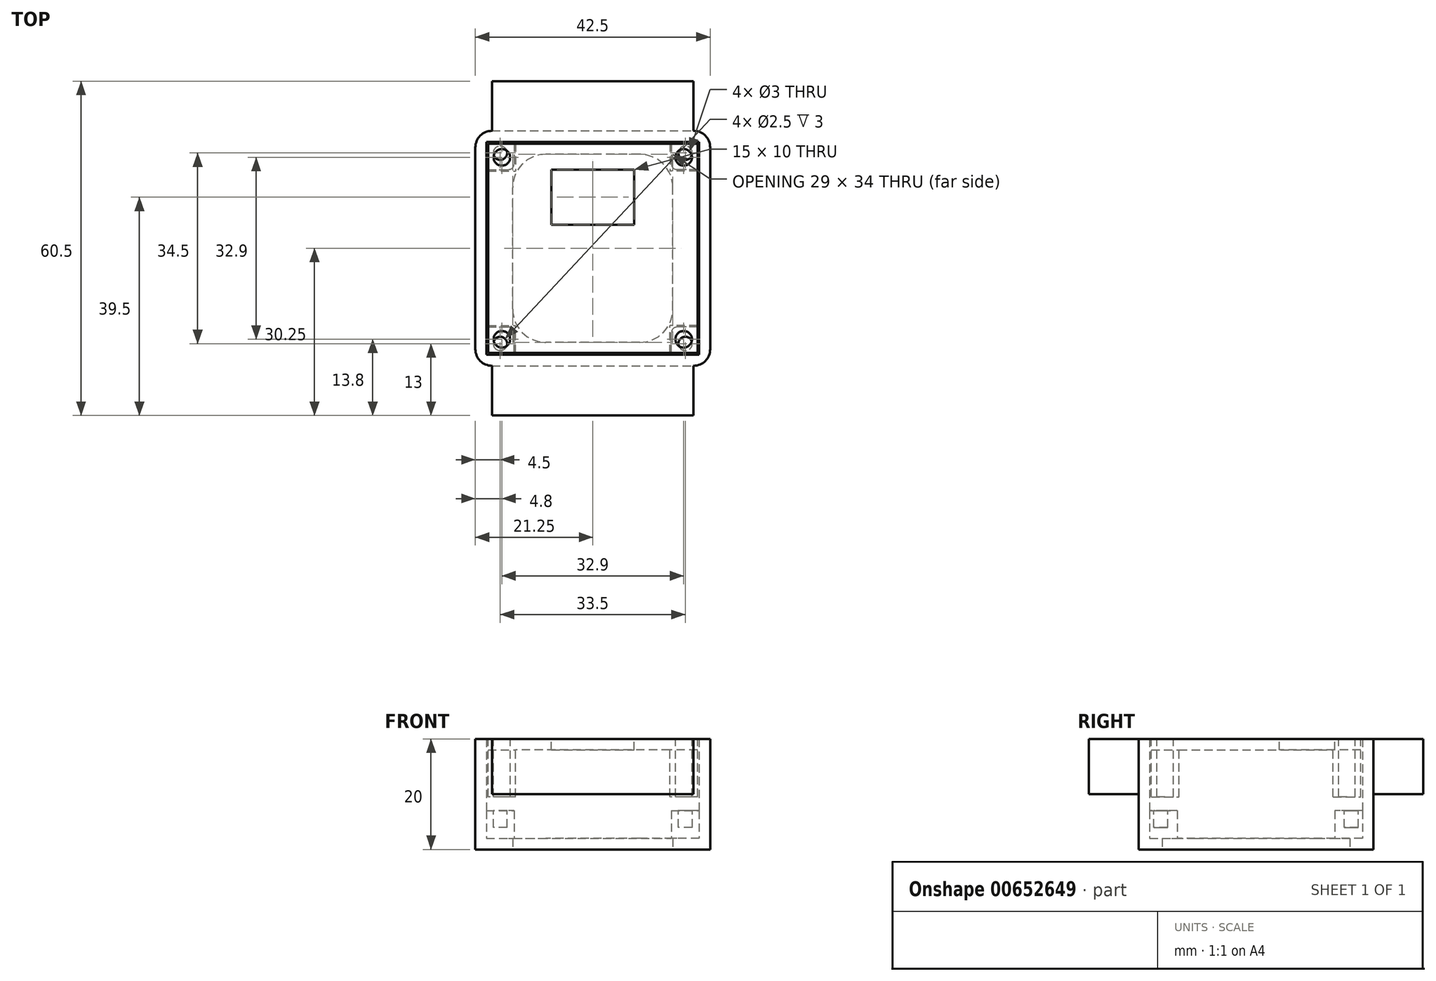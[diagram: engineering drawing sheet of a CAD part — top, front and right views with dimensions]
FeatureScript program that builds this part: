
annotation { "Feature Type Name" : "Feature", "Feature Type Description" : "" }
export const myFeature = defineFeature(function(context is Context, id is Id, definition is map)
    precondition{}
    {
        {
            var Q0;
            Q0=qCreatedBy(makeId("Top.planeOp"),FACE);
            var sketch = newSketch(context, id + "F0", { "sketchPlane" : qUnion([Q0])});
            skLineSegment(sketch, "E0.bottom", {"start": v(19.25, -19.25) * mm, "end": v(-19.25, -19.25) * mm});
            skLineSegment(sketch, "E0.top", {"start": v(19.25, 19.25) * mm, "end": v(-19.25, 19.25) * mm});
            skLineSegment(sketch, "E0.left", {"start": v(19.25, -19.25) * mm, "end": v(19.25, 19.25) * mm});
            skLineSegment(sketch, "E0.right", {"start": v(-19.25, -19.25) * mm, "end": v(-19.25, 19.25) * mm});
            skPoint(sketch, "E0.middle", {"position": v(0, 0) * mm});
            skLineSegment(sketch, "E1.bottom", {"start": v(8.5, -17) * mm, "end": v(-8.5, -17) * mm});
            skLineSegment(sketch, "E1.top", {"start": v(8.5, 17) * mm, "end": v(-8.5, 17) * mm});
            skLineSegment(sketch, "E1.left", {"start": v(14.5, -11) * mm, "end": v(14.5, 11) * mm});
            skLineSegment(sketch, "E1.right", {"start": v(-14.5, -11) * mm, "end": v(-14.5, 11) * mm});
            skLineSegment(sketch, "E2.0", {"start": v(-21.25, -21.25) * mm, "end": v(-21.25, 21.25) * mm});
            skLineSegment(sketch, "E2.1", {"start": v(21.25, -21.25) * mm, "end": v(-21.25, -21.25) * mm});
            skLineSegment(sketch, "E2.2", {"start": v(21.25, -21.25) * mm, "end": v(21.25, 21.25) * mm});
            skLineSegment(sketch, "E2.3", {"start": v(21.25, 21.25) * mm, "end": v(-21.25, 21.25) * mm});
            skPoint(sketch, "E3.visualSharp", {"position": v(-14.5, 17) * mm});
            skArc(sketch, "E3.filletArc", {"start": v(-8.5, 17) * mm, "mid": v(-12.74, 15.24) * mm, "end": v(-14.5, 11) * mm});
            skPoint(sketch, "E4.visualSharp", {"position": v(14.5, 17) * mm});
            skArc(sketch, "E4.filletArc", {"start": v(14.5, 11) * mm, "mid": v(12.74, 15.24) * mm, "end": v(8.5, 17) * mm});
            skPoint(sketch, "E5.visualSharp", {"position": v(14.5, -17) * mm});
            skArc(sketch, "E5.filletArc", {"start": v(8.5, -17) * mm, "mid": v(12.74, -15.24) * mm, "end": v(14.5, -11) * mm});
            skPoint(sketch, "E6.visualSharp", {"position": v(-14.5, -17) * mm});
            skArc(sketch, "E6.filletArc", {"start": v(-14.5, -11) * mm, "mid": v(-12.74, -15.24) * mm, "end": v(-8.5, -17) * mm});
            skSolve(sketch);
        }
        {
            var Q0;
            Q0 = qSketchRegion(id + "F0", true);
            var Q1;
            Q1=makeQuery(id+"F0.imprint","IMPRINT",FACE,{"disambiguationData":[TD([[makeQuery(id+"F0.imprint","IMPRINT",EDGE,{"derivedFrom":sQuery(id+"F0.wireOp",EDGE,"E0.bottom")}),-1.0]])]});
            extrude(context, id + "F1", {"entities" : qUnion([Q0, Q1]), "depth" : 2 * mm, "offsetDistance" : 25 * mm});
        }
        {
            var Q0;
            Q0=makeQuery(id+"F0.imprint","IMPRINT",FACE,{"disambiguationData":[TD([[makeQuery(id+"F0.imprint","IMPRINT",EDGE,{"derivedFrom":sQuery(id+"F0.wireOp",EDGE,"E0.bottom")}),1.0]])]});
            extrude(context, id + "F2", {"entities" : qUnion([Q0]), "operationType" : NewBodyOperationType.ADD, "depth" : 15 * mm, "offsetDistance" : 25 * mm});
        }
        {
            var Q0;
            Q0=makeQuery(id+"F1.opExtrude","CAP_FACE",FACE,{"disambiguationData":[OSD([sQuery(id+"F0.wireOp",EDGE,"E1.bottom"),sQuery(id+"F0.wireOp",EDGE,"E1.top"),sQuery(id+"F0.wireOp",EDGE,"E1.left"),sQuery(id+"F0.wireOp",EDGE,"E1.right"),sQuery(id+"F0.wireOp",EDGE,"E2.0"),sQuery(id+"F0.wireOp",EDGE,"E2.1"),sQuery(id+"F0.wireOp",EDGE,"E2.2"),sQuery(id+"F0.wireOp",EDGE,"E2.3"),sQuery(id+"F0.wireOp",EDGE,"E3.filletArc"),sQuery(id+"F0.wireOp",EDGE,"E4.filletArc"),sQuery(id+"F0.wireOp",EDGE,"E5.filletArc"),sQuery(id+"F0.wireOp",EDGE,"E6.filletArc")])],"isStart":false});
            var sketch = newSketch(context, id + "F3", { "sketchPlane" : qUnion([Q0])});
            skLineSegment(sketch, "E7.bottom", {"start": v(19.25, 19.25) * mm, "end": v(14.25, 19.25) * mm});
            skLineSegment(sketch, "E7.top", {"start": v(19.25, 14.25) * mm, "end": v(14.25, 14.25) * mm});
            skLineSegment(sketch, "E7.left", {"start": v(19.25, 19.25) * mm, "end": v(19.25, 14.25) * mm});
            skLineSegment(sketch, "E7.right", {"start": v(14.25, 19.25) * mm, "end": v(14.25, 14.25) * mm});
            skLineSegment(sketch, "E8.bottom", {"start": v(19.25, -19.25) * mm, "end": v(14.25, -19.25) * mm});
            skLineSegment(sketch, "E8.top", {"start": v(19.25, -14.25) * mm, "end": v(14.25, -14.25) * mm});
            skLineSegment(sketch, "E8.left", {"start": v(19.25, -19.25) * mm, "end": v(19.25, -14.25) * mm});
            skLineSegment(sketch, "E8.right", {"start": v(14.25, -19.25) * mm, "end": v(14.25, -14.25) * mm});
            skLineSegment(sketch, "E9.bottom", {"start": v(-19.25, -19.25) * mm, "end": v(-14.25, -19.25) * mm});
            skLineSegment(sketch, "E9.top", {"start": v(-19.25, -14.25) * mm, "end": v(-14.25, -14.25) * mm});
            skLineSegment(sketch, "E9.left", {"start": v(-19.25, -19.25) * mm, "end": v(-19.25, -14.25) * mm});
            skLineSegment(sketch, "E9.right", {"start": v(-14.25, -19.25) * mm, "end": v(-14.25, -14.25) * mm});
            skLineSegment(sketch, "E10.bottom", {"start": v(-19.25, 19.25) * mm, "end": v(-14.25, 19.25) * mm});
            skLineSegment(sketch, "E10.top", {"start": v(-19.25, 14.25) * mm, "end": v(-14.25, 14.25) * mm});
            skLineSegment(sketch, "E10.left", {"start": v(-19.25, 19.25) * mm, "end": v(-19.25, 14.25) * mm});
            skLineSegment(sketch, "E10.right", {"start": v(-14.25, 19.25) * mm, "end": v(-14.25, 14.25) * mm});
            skSolve(sketch);
        }
        {
            var Q0;
            Q0 = qSketchRegion(id + "F3", true);
            extrude(context, id + "F4", {"entities" : qUnion([Q0]), "operationType" : NewBodyOperationType.ADD, "depth" : 5 * mm, "offsetDistance" : 25 * mm});
        }
        {
            var Q0;
            Q0=makeQuery(id+"F4.opExtrude","SWEPT_EDGE",EDGE,{"disambiguationData":[OSD([sQuery(id+"F3.wireOp",EDGE,"E7.top"),sQuery(id+"F3.wireOp",EDGE,"E7.right")])]});
            var Q1;
            Q1=makeQuery(id+"F4.opExtrude","SWEPT_EDGE",EDGE,{"disambiguationData":[OSD([sQuery(id+"F3.wireOp",EDGE,"E8.top"),sQuery(id+"F3.wireOp",EDGE,"E8.right")])]});
            var Q2;
            Q2=makeQuery(id+"F4.opExtrude","SWEPT_EDGE",EDGE,{"disambiguationData":[OSD([sQuery(id+"F3.wireOp",EDGE,"E9.top"),sQuery(id+"F3.wireOp",EDGE,"E9.right")])]});
            var Q3;
            Q3=makeQuery(id+"F4.opExtrude","SWEPT_EDGE",EDGE,{"disambiguationData":[OSD([sQuery(id+"F3.wireOp",EDGE,"E10.top"),sQuery(id+"F3.wireOp",EDGE,"E10.right")])]});
            fillet(context, id + "F5", {"entities" : qUnion([Q0, Q1, Q2, Q3]), "radius" : 1 * mm, "tangentPropagation" : true, "allowEdgeOverflow" : false});
        }
        {
            var Q0;
            {var subQ0=sQuery(id+"F0.wireOp",EDGE,"E2.3");var subQ1=sQuery(id+"F0.wireOp",EDGE,"E2.2");Q0=makeQuery(id+"F2.boolean.opBoolean","MERGE",EDGE,{"derivedFrom":[makeQuery(id+"F1.opExtrude","SWEPT_EDGE",EDGE,{"disambiguationData":[OSD([subQ1,subQ0])]}),makeQuery(id+"F2.opExtrude","SWEPT_EDGE",EDGE,{"disambiguationData":[OSD([subQ1,subQ0])]})]});}
            var Q1;
            {var subQ0=sQuery(id+"F0.wireOp",EDGE,"E2.2");var subQ1=sQuery(id+"F0.wireOp",EDGE,"E2.1");Q1=makeQuery(id+"F2.boolean.opBoolean","MERGE",EDGE,{"derivedFrom":[makeQuery(id+"F1.opExtrude","SWEPT_EDGE",EDGE,{"disambiguationData":[OSD([subQ1,subQ0])]}),makeQuery(id+"F2.opExtrude","SWEPT_EDGE",EDGE,{"disambiguationData":[OSD([subQ1,subQ0])]})]});}
            var Q2;
            {var subQ0=sQuery(id+"F0.wireOp",EDGE,"E2.1");var subQ1=sQuery(id+"F0.wireOp",EDGE,"E2.0");Q2=makeQuery(id+"F2.boolean.opBoolean","MERGE",EDGE,{"derivedFrom":[makeQuery(id+"F1.opExtrude","SWEPT_EDGE",EDGE,{"disambiguationData":[OSD([subQ1,subQ0])]}),makeQuery(id+"F2.opExtrude","SWEPT_EDGE",EDGE,{"disambiguationData":[OSD([subQ1,subQ0])]})]});}
            var Q3;
            {var subQ0=sQuery(id+"F0.wireOp",EDGE,"E2.3");var subQ1=sQuery(id+"F0.wireOp",EDGE,"E2.0");Q3=makeQuery(id+"F2.boolean.opBoolean","MERGE",EDGE,{"derivedFrom":[makeQuery(id+"F1.opExtrude","SWEPT_EDGE",EDGE,{"disambiguationData":[OSD([subQ1,subQ0])]}),makeQuery(id+"F2.opExtrude","SWEPT_EDGE",EDGE,{"disambiguationData":[OSD([subQ1,subQ0])]})]});}
            fillet(context, id + "F6", {"entities" : qUnion([Q0, Q1, Q2, Q3]), "radius" : 3 * mm, "tangentPropagation" : true, "allowEdgeOverflow" : false});
        }
        {
            var Q0;
            Q0=makeQuery(id+"F4.opExtrude","CAP_FACE",FACE,{"disambiguationData":[OSD([sQuery(id+"F3.wireOp",EDGE,"E8.bottom"),sQuery(id+"F3.wireOp",EDGE,"E8.top"),sQuery(id+"F3.wireOp",EDGE,"E8.left"),sQuery(id+"F3.wireOp",EDGE,"E8.right")])],"isStart":false});
            var sketch = newSketch(context, id + "F7", { "sketchPlane" : qUnion([Q0])});
            skCircle(sketch, "E11", {"center": v(16.75, -17.25) * mm, "radius": 1.25 * mm});
            skPoint(sketch, "E11.centerSnap0", {"position": v(16.75, -19.25) * mm});
            skPoint(sketch, "E11.centerSnap1", {"position": v(14.25, -17.25) * mm});
            skCircle(sketch, "E12.MirrorC", {"center": v(-16.75, -17.25) * mm, "radius": 1.25 * mm});
            skCircle(sketch, "E13.MirrorC", {"center": v(16.75, 17.25) * mm, "radius": 1.25 * mm});
            skCircle(sketch, "E14.MirrorC", {"center": v(-16.75, 17.25) * mm, "radius": 1.25 * mm});
            skSolve(sketch);
        }
        {
            var Q0;
            Q0 = qSketchRegion(id + "F7", true);
            extrude(context, id + "F8", {"entities" : qUnion([Q0]), "operationType" : NewBodyOperationType.REMOVE, "oppositeDirection" : true, "depth" : 3 * mm, "offsetDistance" : 25 * mm});
        }
        {
            var Q0;
            Q0=makeQuery(id+"F2.opExtrude","CAP_FACE",FACE,{"disambiguationData":[OSD([sQuery(id+"F0.wireOp",EDGE,"E0.bottom"),sQuery(id+"F0.wireOp",EDGE,"E0.top"),sQuery(id+"F0.wireOp",EDGE,"E0.left"),sQuery(id+"F0.wireOp",EDGE,"E0.right"),sQuery(id+"F0.wireOp",EDGE,"E2.0"),sQuery(id+"F0.wireOp",EDGE,"E2.1"),sQuery(id+"F0.wireOp",EDGE,"E2.2"),sQuery(id+"F0.wireOp",EDGE,"E2.3")])],"isStart":false});
            extrude(context, id + "F9", {"entities" : qUnion([Q0]), "operationType" : NewBodyOperationType.ADD, "depth" : 5 * mm, "offsetDistance" : 25 * mm});
        }
        {
            var Q0;
            Q0=makeQuery(id+"F9.opExtrude","CAP_FACE",FACE,{"disambiguationData":[OSD([sQuery(id+"F0.wireOp",EDGE,"E0.bottom"),sQuery(id+"F0.wireOp",EDGE,"E0.top"),sQuery(id+"F0.wireOp",EDGE,"E0.left"),sQuery(id+"F0.wireOp",EDGE,"E0.right"),sQuery(id+"F0.wireOp",EDGE,"E2.0"),sQuery(id+"F0.wireOp",EDGE,"E2.1"),sQuery(id+"F0.wireOp",EDGE,"E2.2"),sQuery(id+"F0.wireOp",EDGE,"E2.3")])],"isStart":false});
            var sketch = newSketch(context, id + "F10", { "sketchPlane" : qUnion([Q0])});
            skLineSegment(sketch, "E15.0", {"start": v(18.25, -21.25) * mm, "end": v(-18.25, -21.25) * mm});
            skLineSegment(sketch, "E15.1", {"start": v(21.25, -18.25) * mm, "end": v(21.25, 18.25) * mm});
            skLineSegment(sketch, "E15.2", {"start": v(18.25, 21.25) * mm, "end": v(-18.25, 21.25) * mm});
            skLineSegment(sketch, "E15.3", {"start": v(-21.25, -18.25) * mm, "end": v(-21.25, 18.25) * mm});
            skPoint(sketch, "E16.visualSharp", {"position": v(21.25, -21.25) * mm});
            skArc(sketch, "E16.filletArc", {"start": v(18.25, -21.25) * mm, "mid": v(20.37, -20.37) * mm, "end": v(21.25, -18.25) * mm});
            skPoint(sketch, "E17.visualSharp", {"position": v(-21.25, -21.25) * mm});
            skArc(sketch, "E17.filletArc", {"start": v(-21.25, -18.25) * mm, "mid": v(-20.37, -20.37) * mm, "end": v(-18.25, -21.25) * mm});
            skPoint(sketch, "E18.visualSharp", {"position": v(-21.25, 21.25) * mm});
            skArc(sketch, "E18.filletArc", {"start": v(-18.25, 21.25) * mm, "mid": v(-20.37, 20.37) * mm, "end": v(-21.25, 18.25) * mm});
            skPoint(sketch, "E19.visualSharp", {"position": v(21.25, 21.25) * mm});
            skArc(sketch, "E19.filletArc", {"start": v(21.25, 18.25) * mm, "mid": v(20.37, 20.37) * mm, "end": v(18.25, 21.25) * mm});
            skLineSegment(sketch, "E20.bottom", {"start": v(19.25, -19.25) * mm, "end": v(-19.25, -19.25) * mm});
            skLineSegment(sketch, "E20.top", {"start": v(19.25, 19.25) * mm, "end": v(-19.25, 19.25) * mm});
            skLineSegment(sketch, "E20.left", {"start": v(19.25, -19.25) * mm, "end": v(19.25, 19.25) * mm});
            skLineSegment(sketch, "E20.right", {"start": v(-19.25, -19.25) * mm, "end": v(-19.25, 19.25) * mm});
            skLineSegment(sketch, "E21.0", {"start": v(18.95, -18.95) * mm, "end": v(18.95, 18.95) * mm});
            skLineSegment(sketch, "E21.1", {"start": v(18.95, -18.95) * mm, "end": v(-18.95, -18.95) * mm});
            skLineSegment(sketch, "E21.2", {"start": v(-18.95, -18.95) * mm, "end": v(-18.95, 18.95) * mm});
            skLineSegment(sketch, "E21.3", {"start": v(18.95, 18.95) * mm, "end": v(-18.95, 18.95) * mm});
            skLineSegment(sketch, "E22.bottom", {"start": v(-7.5, 14.25) * mm, "end": v(7.5, 14.25) * mm});
            skLineSegment(sketch, "E22.top", {"start": v(-7.5, 4.25) * mm, "end": v(7.5, 4.25) * mm});
            skLineSegment(sketch, "E22.left", {"start": v(-7.5, 14.25) * mm, "end": v(-7.5, 4.25) * mm});
            skLineSegment(sketch, "E22.right", {"start": v(7.5, 14.25) * mm, "end": v(7.5, 4.25) * mm});
            skPoint(sketch, "E22.middle", {"position": v(0, 9.25) * mm});
            skSolve(sketch);
        }
        {
            var Q0;
            Q0=makeQuery(id+"F10.imprint","IMPRINT",FACE,{"disambiguationData":[TD([[makeQuery(id+"F10.imprint","IMPRINT",EDGE,{"derivedFrom":sQuery(id+"F10.wireOp",EDGE,"E21.0")}),1.0]])]});
            extrude(context, id + "F11", {"entities" : qUnion([Q0]), "oppositeDirection" : true, "depth" : 2 * mm, "offsetDistance" : 25 * mm});
        }
        {
            var Q0;
            Q0=makeQuery(id+"F11.opExtrude","CAP_FACE",FACE,{"disambiguationData":[OSD([sQuery(id+"F10.wireOp",EDGE,"E21.0"),sQuery(id+"F10.wireOp",EDGE,"E21.1"),sQuery(id+"F10.wireOp",EDGE,"E21.2"),sQuery(id+"F10.wireOp",EDGE,"E21.3"),sQuery(id+"F10.wireOp",EDGE,"E22.bottom"),sQuery(id+"F10.wireOp",EDGE,"E22.top"),sQuery(id+"F10.wireOp",EDGE,"E22.left"),sQuery(id+"F10.wireOp",EDGE,"E22.right")])],"isStart":false});
            var sketch = newSketch(context, id + "F12", { "sketchPlane" : qUnion([Q0])});
            skLineSegment(sketch, "E23.bottom", {"start": v(-18.95, 18.95) * mm, "end": v(-13.95, 18.95) * mm});
            skLineSegment(sketch, "E23.top", {"start": v(-18.95, 13.95) * mm, "end": v(-13.95, 13.95) * mm});
            skLineSegment(sketch, "E23.left", {"start": v(-18.95, 18.95) * mm, "end": v(-18.95, 13.95) * mm});
            skLineSegment(sketch, "E23.right", {"start": v(-13.95, 18.95) * mm, "end": v(-13.95, 13.95) * mm});
            skLineSegment(sketch, "E24.MirrorCS", {"start": v(13.95, 18.95) * mm, "end": v(13.95, 13.95) * mm});
            skLineSegment(sketch, "E25.MirrorCS", {"start": v(18.95, 18.95) * mm, "end": v(18.95, 13.95) * mm});
            skLineSegment(sketch, "E26.MirrorCS", {"start": v(18.95, 13.95) * mm, "end": v(13.95, 13.95) * mm});
            skLineSegment(sketch, "E27.MirrorCS", {"start": v(18.95, 18.95) * mm, "end": v(13.95, 18.95) * mm});
            skLineSegment(sketch, "E28.MirrorCS", {"start": v(-13.95, -18.95) * mm, "end": v(-13.95, -13.95) * mm});
            skLineSegment(sketch, "E29.MirrorCS", {"start": v(-18.95, -18.95) * mm, "end": v(-18.95, -13.95) * mm});
            skLineSegment(sketch, "E30.MirrorCS", {"start": v(-18.95, -13.95) * mm, "end": v(-13.95, -13.95) * mm});
            skLineSegment(sketch, "E31.MirrorCS", {"start": v(-18.95, -18.95) * mm, "end": v(-13.95, -18.95) * mm});
            skLineSegment(sketch, "E32.MirrorCS", {"start": v(13.95, -18.95) * mm, "end": v(13.95, -13.95) * mm});
            skLineSegment(sketch, "E33.MirrorCS", {"start": v(18.95, -18.95) * mm, "end": v(18.95, -13.95) * mm});
            skLineSegment(sketch, "E34.MirrorCS", {"start": v(18.95, -13.95) * mm, "end": v(13.95, -13.95) * mm});
            skLineSegment(sketch, "E35.MirrorCS", {"start": v(18.95, -18.95) * mm, "end": v(13.95, -18.95) * mm});
            skCircle(sketch, "E36", {"center": v(-16.45, 16.45) * mm, "radius": 1.5 * mm});
            skPoint(sketch, "E36.centerSnap0", {"position": v(-16.45, 18.95) * mm});
            skPoint(sketch, "E36.centerSnap1", {"position": v(-13.95, 16.45) * mm});
            skCircle(sketch, "E37.MirrorC", {"center": v(16.45, 16.45) * mm, "radius": 1.5 * mm});
            skCircle(sketch, "E38.MirrorC", {"center": v(-16.45, -16.45) * mm, "radius": 1.5 * mm});
            skCircle(sketch, "E39.MirrorC", {"center": v(16.45, -16.45) * mm, "radius": 1.5 * mm});
            skSolve(sketch);
        }
        {
            var Q0;
            Q0 = qSketchRegion(id + "F12", true);
            extrude(context, id + "F13", {"entities" : qUnion([Q0]), "operationType" : NewBodyOperationType.ADD, "depth" : 8.5 * mm, "offsetDistance" : 25 * mm});
        }
        {
            var Q0;
            Q0=makeQuery(id+"F13.boolean.opBoolean","SPLIT",FACE,{"disambiguationData":[TD([makeQuery(id+"F13.opExtrude","SWEPT_FACE",FACE,{"disambiguationData":[OSD([sQuery(id+"F12.wireOp",EDGE,"E36")])]})])],"derivedFrom":makeQuery(id+"F11.opExtrude","CAP_FACE",FACE,{"disambiguationData":[OSD([sQuery(id+"F10.wireOp",EDGE,"E21.0"),sQuery(id+"F10.wireOp",EDGE,"E21.1"),sQuery(id+"F10.wireOp",EDGE,"E21.2"),sQuery(id+"F10.wireOp",EDGE,"E21.3"),sQuery(id+"F10.wireOp",EDGE,"E22.bottom"),sQuery(id+"F10.wireOp",EDGE,"E22.top"),sQuery(id+"F10.wireOp",EDGE,"E22.left"),sQuery(id+"F10.wireOp",EDGE,"E22.right")])],"isStart":false})});
            var Q1;
            Q1=makeQuery(id+"F13.boolean.opBoolean","SPLIT",FACE,{"disambiguationData":[TD([makeQuery(id+"F13.opExtrude","SWEPT_FACE",FACE,{"disambiguationData":[OSD([sQuery(id+"F12.wireOp",EDGE,"E37.MirrorC")])]})])],"derivedFrom":makeQuery(id+"F11.opExtrude","CAP_FACE",FACE,{"disambiguationData":[OSD([sQuery(id+"F10.wireOp",EDGE,"E21.0"),sQuery(id+"F10.wireOp",EDGE,"E21.1"),sQuery(id+"F10.wireOp",EDGE,"E21.2"),sQuery(id+"F10.wireOp",EDGE,"E21.3"),sQuery(id+"F10.wireOp",EDGE,"E22.bottom"),sQuery(id+"F10.wireOp",EDGE,"E22.top"),sQuery(id+"F10.wireOp",EDGE,"E22.left"),sQuery(id+"F10.wireOp",EDGE,"E22.right")])],"isStart":false})});
            var Q2;
            Q2=makeQuery(id+"F13.boolean.opBoolean","SPLIT",FACE,{"disambiguationData":[TD([makeQuery(id+"F13.opExtrude","SWEPT_FACE",FACE,{"disambiguationData":[OSD([sQuery(id+"F12.wireOp",EDGE,"E39.MirrorC")])]})])],"derivedFrom":makeQuery(id+"F11.opExtrude","CAP_FACE",FACE,{"disambiguationData":[OSD([sQuery(id+"F10.wireOp",EDGE,"E21.0"),sQuery(id+"F10.wireOp",EDGE,"E21.1"),sQuery(id+"F10.wireOp",EDGE,"E21.2"),sQuery(id+"F10.wireOp",EDGE,"E21.3"),sQuery(id+"F10.wireOp",EDGE,"E22.bottom"),sQuery(id+"F10.wireOp",EDGE,"E22.top"),sQuery(id+"F10.wireOp",EDGE,"E22.left"),sQuery(id+"F10.wireOp",EDGE,"E22.right")])],"isStart":false})});
            var Q3;
            Q3=makeQuery(id+"F13.boolean.opBoolean","SPLIT",FACE,{"disambiguationData":[TD([makeQuery(id+"F13.opExtrude","SWEPT_FACE",FACE,{"disambiguationData":[OSD([sQuery(id+"F12.wireOp",EDGE,"E38.MirrorC")])]})])],"derivedFrom":makeQuery(id+"F11.opExtrude","CAP_FACE",FACE,{"disambiguationData":[OSD([sQuery(id+"F10.wireOp",EDGE,"E21.0"),sQuery(id+"F10.wireOp",EDGE,"E21.1"),sQuery(id+"F10.wireOp",EDGE,"E21.2"),sQuery(id+"F10.wireOp",EDGE,"E21.3"),sQuery(id+"F10.wireOp",EDGE,"E22.bottom"),sQuery(id+"F10.wireOp",EDGE,"E22.top"),sQuery(id+"F10.wireOp",EDGE,"E22.left"),sQuery(id+"F10.wireOp",EDGE,"E22.right")])],"isStart":false})});
            extrude(context, id + "F14", {"entities" : qUnion([Q0, Q1, Q2, Q3]), "operationType" : NewBodyOperationType.REMOVE, "oppositeDirection" : true, "depth" : 25 * mm, "offsetDistance" : 25 * mm});
        }
        {
            var Q0;
            {var subQ0=sQuery(id+"F0.wireOp",EDGE,"E2.1");Q0=makeQuery(id+"F9.boolean.opBoolean","MERGE",FACE,{"derivedFrom":[makeQuery(id+"F2.boolean.opBoolean","MERGE",FACE,{"derivedFrom":[makeQuery(id+"F1.opExtrude","SWEPT_FACE",FACE,{"disambiguationData":[OSD([subQ0])]}),makeQuery(id+"F2.opExtrude","SWEPT_FACE",FACE,{"disambiguationData":[OSD([subQ0])]})]}),makeQuery(id+"F9.opExtrude","SWEPT_FACE",FACE,{"disambiguationData":[OSD([subQ0])]})]});}
            var sketch = newSketch(context, id + "F15", { "sketchPlane" : qUnion([Q0])});
            skLineSegment(sketch, "E40.bottom", {"start": v(-18.25, 20) * mm, "end": v(18.25, 20) * mm});
            skLineSegment(sketch, "E40.top", {"start": v(-18.25, 10) * mm, "end": v(18.25, 10) * mm});
            skLineSegment(sketch, "E40.left", {"start": v(-18.25, 20) * mm, "end": v(-18.25, 10) * mm});
            skLineSegment(sketch, "E40.right", {"start": v(18.25, 20) * mm, "end": v(18.25, 10) * mm});
            skSolve(sketch);
        }
        {
            var Q0;
            Q0 = qSketchRegion(id + "F15", true);
            extrude(context, id + "F16", {"entities" : qUnion([Q0]), "operationType" : NewBodyOperationType.ADD, "depth" : 9 * mm, "offsetDistance" : 25 * mm});
        }
        {
            var Q0;
            {var subQ0=sQuery(id+"F0.wireOp",EDGE,"E2.3");Q0=makeQuery(id+"F9.boolean.opBoolean","MERGE",FACE,{"derivedFrom":[makeQuery(id+"F2.boolean.opBoolean","MERGE",FACE,{"derivedFrom":[makeQuery(id+"F1.opExtrude","SWEPT_FACE",FACE,{"disambiguationData":[OSD([subQ0])]}),makeQuery(id+"F2.opExtrude","SWEPT_FACE",FACE,{"disambiguationData":[OSD([subQ0])]})]}),makeQuery(id+"F9.opExtrude","SWEPT_FACE",FACE,{"disambiguationData":[OSD([subQ0])]})]});}
            var sketch = newSketch(context, id + "F17", { "sketchPlane" : qUnion([Q0])});
            skLineSegment(sketch, "E41.bottom", {"start": v(18.25, 20) * mm, "end": v(-18.25, 20) * mm});
            skLineSegment(sketch, "E41.top", {"start": v(18.25, 10) * mm, "end": v(-18.25, 10) * mm});
            skLineSegment(sketch, "E41.left", {"start": v(18.25, 20) * mm, "end": v(18.25, 10) * mm});
            skLineSegment(sketch, "E41.right", {"start": v(-18.25, 20) * mm, "end": v(-18.25, 10) * mm});
            skSolve(sketch);
        }
        {
            var Q0;
            Q0=makeQuery(id+"F17.imprint","IMPRINT",FACE,{"disambiguationData":[TD([[makeQuery(id+"F17.imprint","IMPRINT",EDGE,{"derivedFrom":sQuery(id+"F17.wireOp",EDGE,"E41.bottom")}),-1.0]])]});
            extrude(context, id + "F18", {"entities" : qUnion([Q0]), "operationType" : NewBodyOperationType.ADD, "depth" : 9 * mm, "offsetDistance" : 25 * mm});
        }
    });
